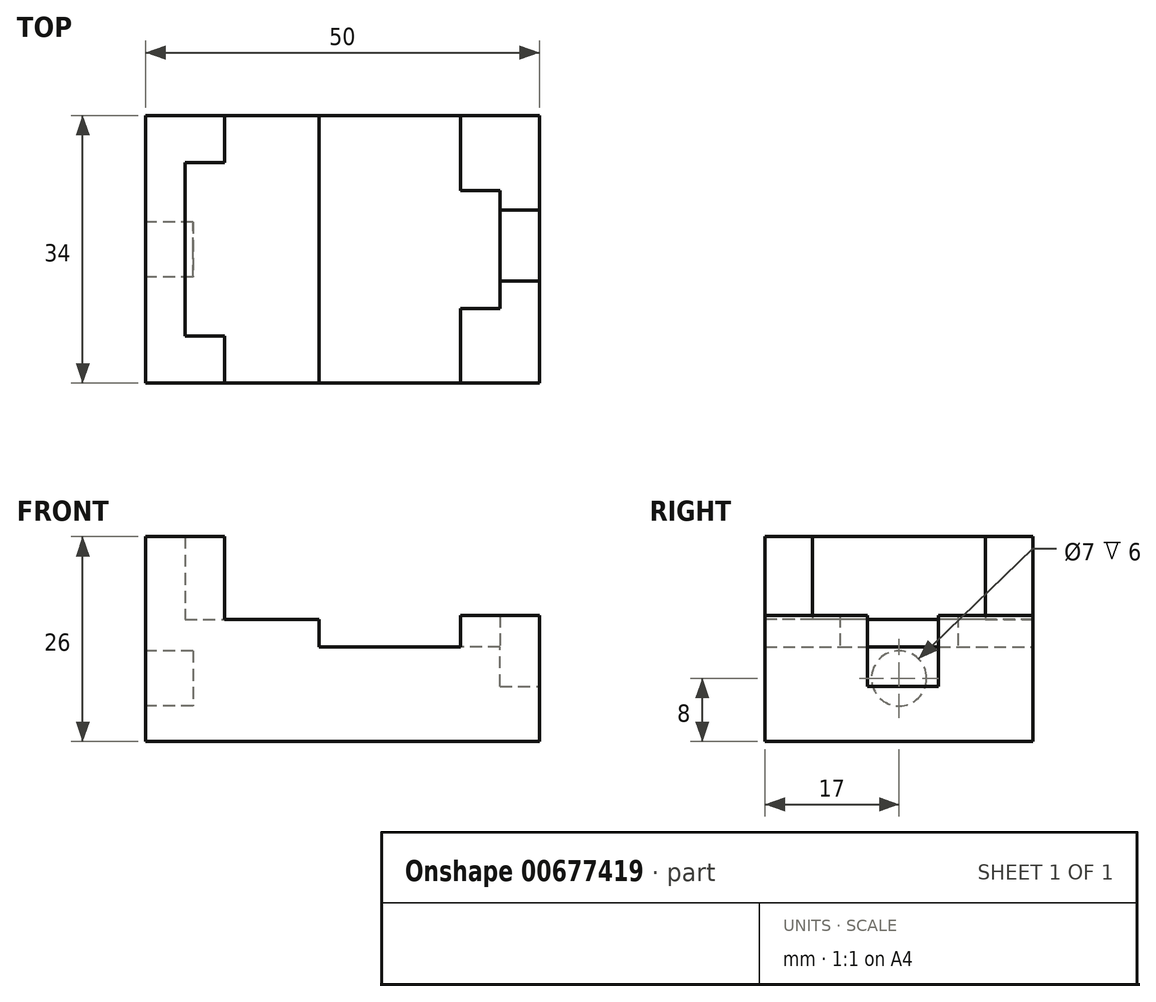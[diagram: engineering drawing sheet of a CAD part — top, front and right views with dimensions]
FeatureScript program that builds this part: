
annotation { "Feature Type Name" : "Feature", "Feature Type Description" : "" }
export const myFeature = defineFeature(function(context is Context, id is Id, definition is map)
    precondition{}
    {
        {
            var Q0;
            Q0=qCreatedBy(makeId("Front.planeOp"),FACE);
            var sketch = newSketch(context, id + "F0", { "sketchPlane" : qUnion([Q0])});
            skLineSegment(sketch, "E0.bottom", {"start": v(-25, 13) * mm, "end": v(0.85, 13) * mm});
            skLineSegment(sketch, "E0.top", {"start": v(-25, -13) * mm, "end": v(25, -13) * mm});
            skLineSegment(sketch, "E0.left", {"start": v(-25, 13) * mm, "end": v(-25, -13) * mm});
            skLineSegment(sketch, "E0.right", {"start": v(25, 3) * mm, "end": v(25, -13) * mm});
            skPoint(sketch, "E0.middle", {"position": v(0, 0) * mm});
            skLineSegment(sketch, "E1.0", {"start": v(0.85, 13) * mm, "end": v(0.85, -1) * mm});
            skLineSegment(sketch, "E2.0", {"start": v(0.85, -1) * mm, "end": v(20, -1) * mm});
            skLineSegment(sketch, "E3.0", {"start": v(20, 3) * mm, "end": v(20, -1) * mm});
            skPoint(sketch, "E4.orphan", {"position": v(25, 13) * mm});
            skLineSegment(sketch, "E5.trimOffspring", {"start": v(20, 3) * mm, "end": v(25, 3) * mm});
            skSolve(sketch);
        }
        {
            var Q0;
            Q0=qSketchRegion(id+"F0",true);
            extrude(context, id + "F1", {"entities" : qUnion([Q0]), "depth" : 34 * mm, "offsetDistance" : 25 * mm});
        }
        {
            var Q0;
            Q0=makeQuery(id+"F1.opExtrude","SWEPT_FACE",FACE,{"disambiguationData":[OSD([sQuery(id+"F0.wireOp",EDGE,"E0.right")])]});
            var sketch = newSketch(context, id + "F2", { "sketchPlane" : qUnion([Q0])});
            skLineSegment(sketch, "E6.bottom", {"start": v(-21, 3) * mm, "end": v(-12, 3) * mm});
            skLineSegment(sketch, "E6.top", {"start": v(-21, -6) * mm, "end": v(-12, -6) * mm});
            skLineSegment(sketch, "E6.left", {"start": v(-21, 3) * mm, "end": v(-21, -6) * mm});
            skLineSegment(sketch, "E7", {"start": v(-12, 3) * mm, "end": v(-12, -6) * mm});
            skSolve(sketch);
        }
        {
            var Q0;
            Q0=qSketchRegion(id+"F2",true);
            var Q1;
            Q1=makeQuery(id+"F1.opExtrude","SWEPT_FACE",FACE,{"disambiguationData":[OSD([sQuery(id+"F0.wireOp",EDGE,"E3.0")])]});
            extrude(context, id + "F3", {"entities" : qUnion([Q0]), "operationType" : NewBodyOperationType.REMOVE, "endBound" : BoundingType.UP_TO_SURFACE, "oppositeDirection" : true, "depth" : 25 * mm, "endBoundEntityFace" : qUnion([Q1]), "offsetDistance" : 25 * mm});
        }
        {
            var Q0;
            Q0=makeQuery(id+"F1.opExtrude","SWEPT_FACE",FACE,{"disambiguationData":[OSD([sQuery(id+"F0.wireOp",EDGE,"E0.left")])]});
            var sketch = newSketch(context, id + "F4", { "sketchPlane" : qUnion([Q0])});
            skCircle(sketch, "E8", {"center": v(17, -5) * mm, "radius": 3.5 * mm});
            skSolve(sketch);
        }
        {
            var Q0;
            Q0=qSketchRegion(id+"F4",true);
            extrude(context, id + "F5", {"entities" : qUnion([Q0]), "operationType" : NewBodyOperationType.REMOVE, "oppositeDirection" : true, "depth" : 6 * mm, "offsetDistance" : 25 * mm});
        }
        {
            var Q0;
            Q0=makeQuery(id+"F3.boolean.opBoolean","MERGE",FACE,{"derivedFrom":[makeQuery(id+"F1.opExtrude","SWEPT_FACE",FACE,{"disambiguationData":[OSD([sQuery(id+"F0.wireOp",EDGE,"E2.0")])]}),makeQuery(id+"F3.opExtrude","SWEPT_FACE",FACE,{"disambiguationData":[OSD([sQuery(id+"F2.wireOp",EDGE,"E6.top")])]})]});
            var sketch = newSketch(context, id + "F6", { "sketchPlane" : qUnion([Q0])});
            skLineSegment(sketch, "E9.bottom", {"start": v(20, -34) * mm, "end": v(15, -34) * mm});
            skLineSegment(sketch, "E9.top", {"start": v(20, -24.5) * mm, "end": v(15, -24.5) * mm});
            skLineSegment(sketch, "E9.left", {"start": v(20, -34) * mm, "end": v(20, -24.5) * mm});
            skLineSegment(sketch, "E9.right", {"start": v(15, -34) * mm, "end": v(15, -24.5) * mm});
            skLineSegment(sketch, "E10.bottom", {"start": v(20, -9.5) * mm, "end": v(15, -9.5) * mm});
            skLineSegment(sketch, "E10.top", {"start": v(20, 0) * mm, "end": v(15, 0) * mm});
            skLineSegment(sketch, "E10.left", {"start": v(20, -9.5) * mm, "end": v(20, 0) * mm});
            skLineSegment(sketch, "E10.right", {"start": v(15, -9.5) * mm, "end": v(15, 0) * mm});
            skSolve(sketch);
        }
        {
            var Q0;
            Q0=qSketchRegion(id+"F6",true);
            var Q1;
            {var subQ0=sQuery(id+"F0.wireOp",EDGE,"E5.trimOffspring");Q1=makeQuery(id+"F3.boolean.opBoolean","SPLIT",FACE,{"disambiguationData":[TD([makeQuery(id+"F3.opExtrude","SWEPT_FACE",FACE,{"disambiguationData":[OSD([sQuery(id+"F2.wireOp",EDGE,"E6.left")])]})])],"derivedFrom":makeQuery(id+"F1.opExtrude","SWEPT_FACE",FACE,{"disambiguationData":[OSD([subQ0])]})});}
            extrude(context, id + "F7", {"entities" : qUnion([Q0]), "operationType" : NewBodyOperationType.ADD, "endBound" : BoundingType.UP_TO_SURFACE, "depth" : 25 * mm, "endBoundEntityFace" : qUnion([Q1]), "offsetDistance" : 25 * mm});
        }
        {
            var Q0;
            Q0=makeQuery(id+"F7.boolean.opBoolean","MERGE",FACE,{"derivedFrom":[makeQuery(id+"F1.opExtrude","CAP_FACE",FACE,{"disambiguationData":[OSD([sQuery(id+"F0.wireOp",EDGE,"E0.bottom"),sQuery(id+"F0.wireOp",EDGE,"E0.top"),sQuery(id+"F0.wireOp",EDGE,"E0.left"),sQuery(id+"F0.wireOp",EDGE,"E0.right"),sQuery(id+"F0.wireOp",EDGE,"E1.0"),sQuery(id+"F0.wireOp",EDGE,"E2.0"),sQuery(id+"F0.wireOp",EDGE,"E3.0"),sQuery(id+"F0.wireOp",EDGE,"E5.trimOffspring")])],"isStart":false}),makeQuery(id+"F7.opExtrude","SWEPT_FACE",FACE,{"disambiguationData":[OSD([sQuery(id+"F6.wireOp",EDGE,"E9.bottom")])]})]});
            var sketch = newSketch(context, id + "F8", { "sketchPlane" : qUnion([Q0])});
            skLineSegment(sketch, "E11.bottom", {"start": v(0.85, 13) * mm, "end": v(-20, 13) * mm});
            skLineSegment(sketch, "E11.top", {"start": v(0.85, -1) * mm, "end": v(-20, -1) * mm});
            skLineSegment(sketch, "E11.left", {"start": v(0.85, 13) * mm, "end": v(0.85, -1) * mm});
            skLineSegment(sketch, "E11.right", {"start": v(-20, 13) * mm, "end": v(-20, -1) * mm});
            skSolve(sketch);
        }
        {
            var Q0;
            Q0 = qSketchRegion(id + "F8", true);
            extrude(context, id + "F9", {"entities" : qUnion([Q0]), "operationType" : NewBodyOperationType.REMOVE, "endBound" : BoundingType.THROUGH_ALL, "oppositeDirection" : true, "depth" : 25 * mm, "offsetDistance" : 25 * mm});
        }
        {
            var Q0;
            Q0=makeQuery(id+"F7.boolean.opBoolean","MERGE",FACE,{"derivedFrom":[makeQuery(id+"F1.opExtrude","CAP_FACE",FACE,{"disambiguationData":[OSD([sQuery(id+"F0.wireOp",EDGE,"E0.bottom"),sQuery(id+"F0.wireOp",EDGE,"E0.top"),sQuery(id+"F0.wireOp",EDGE,"E0.left"),sQuery(id+"F0.wireOp",EDGE,"E0.right"),sQuery(id+"F0.wireOp",EDGE,"E1.0"),sQuery(id+"F0.wireOp",EDGE,"E2.0"),sQuery(id+"F0.wireOp",EDGE,"E3.0"),sQuery(id+"F0.wireOp",EDGE,"E5.trimOffspring")])],"isStart":false}),makeQuery(id+"F7.opExtrude","SWEPT_FACE",FACE,{"disambiguationData":[OSD([sQuery(id+"F6.wireOp",EDGE,"E9.bottom")])]})]});
            var sketch = newSketch(context, id + "F10", { "sketchPlane" : qUnion([Q0])});
            skLineSegment(sketch, "E12.bottom", {"start": v(-20, 13) * mm, "end": v(-15, 13) * mm});
            skLineSegment(sketch, "E12.top", {"start": v(-20, -1) * mm, "end": v(-15, -1) * mm});
            skLineSegment(sketch, "E12.left", {"start": v(-20, 13) * mm, "end": v(-20, -1) * mm});
            skLineSegment(sketch, "E12.right", {"start": v(-15, 13) * mm, "end": v(-15, -1) * mm});
            skSolve(sketch);
        }
        {
            var Q0;
            Q0 = qSketchRegion(id + "F10", true);
            extrude(context, id + "F11", {"entities" : qUnion([Q0]), "operationType" : NewBodyOperationType.ADD, "oppositeDirection" : true, "depth" : 6 * mm, "offsetDistance" : 25 * mm});
        }
        {
            var Q0;
            Q0=makeQuery(id+"F7.boolean.opBoolean","MERGE",FACE,{"derivedFrom":[makeQuery(id+"F1.opExtrude","CAP_FACE",FACE,{"disambiguationData":[OSD([sQuery(id+"F0.wireOp",EDGE,"E0.bottom"),sQuery(id+"F0.wireOp",EDGE,"E0.top"),sQuery(id+"F0.wireOp",EDGE,"E0.left"),sQuery(id+"F0.wireOp",EDGE,"E0.right"),sQuery(id+"F0.wireOp",EDGE,"E1.0"),sQuery(id+"F0.wireOp",EDGE,"E2.0"),sQuery(id+"F0.wireOp",EDGE,"E3.0"),sQuery(id+"F0.wireOp",EDGE,"E5.trimOffspring")])],"isStart":true}),makeQuery(id+"F7.opExtrude","SWEPT_FACE",FACE,{"disambiguationData":[OSD([sQuery(id+"F6.wireOp",EDGE,"E10.top")])]})]});
            var sketch = newSketch(context, id + "F12", { "sketchPlane" : qUnion([Q0])});
            skLineSegment(sketch, "E13.bottom", {"start": v(20, 13) * mm, "end": v(15, 13) * mm});
            skLineSegment(sketch, "E13.top", {"start": v(20, -1) * mm, "end": v(15, -1) * mm});
            skLineSegment(sketch, "E13.left", {"start": v(20, 13) * mm, "end": v(20, -1) * mm});
            skLineSegment(sketch, "E13.right", {"start": v(15, 13) * mm, "end": v(15, -1) * mm});
            skSolve(sketch);
        }
        {
            var Q0;
            Q0 = qSketchRegion(id + "F12", true);
            extrude(context, id + "F13", {"entities" : qUnion([Q0]), "operationType" : NewBodyOperationType.ADD, "oppositeDirection" : true, "depth" : 6 * mm, "offsetDistance" : 25 * mm});
        }
        {
            var Q0;
            Q0=makeQuery(id+"F9.boolean.opBoolean","MERGE",FACE,{"derivedFrom":[makeQuery(id+"F1.opExtrude","SWEPT_FACE",FACE,{"disambiguationData":[OSD([sQuery(id+"F0.wireOp",EDGE,"E2.0")])]}),makeQuery(id+"F9.opExtrude","SWEPT_FACE",FACE,{"disambiguationData":[OSD([sQuery(id+"F8.wireOp",EDGE,"E11.top")])]})]});
            var sketch = newSketch(context, id + "F14", { "sketchPlane" : qUnion([Q0])});
            skLineSegment(sketch, "E14.0.0", {"start": v(-15, 0) * mm, "end": v(-15, -6) * mm});
            skLineSegment(sketch, "E14.0.1", {"start": v(-15, -6) * mm, "end": v(-20, -6) * mm});
            skLineSegment(sketch, "E14.0.2", {"start": v(-20, -6) * mm, "end": v(-20, -28) * mm});
            skLineSegment(sketch, "E14.0.3", {"start": v(-20, -28) * mm, "end": v(-15, -28) * mm});
            skLineSegment(sketch, "E14.0.4", {"start": v(-15, -28) * mm, "end": v(-15, -34) * mm});
            skLineSegment(sketch, "E14.0.5", {"start": v(-15, -34) * mm, "end": v(-3, -34) * mm});
            skLineSegment(sketch, "E14.0.10", {"start": v(20, -12) * mm, "end": v(20, -9.5) * mm});
            skLineSegment(sketch, "E14.0.13", {"start": v(-3, 0) * mm, "end": v(-15, 0) * mm});
            skLineSegment(sketch, "E15", {"start": v(-3, 0) * mm, "end": v(-3, -34) * mm});
            skPoint(sketch, "E14.0.12.end.orphan", {"position": v(15, 0) * mm});
            skPoint(sketch, "E14.0.11.end.orphan", {"position": v(15, -9.5) * mm});
            skPoint(sketch, "E14.0.8.end.orphan", {"position": v(20, -21) * mm});
            skPoint(sketch, "E14.0.7.end.orphan", {"position": v(20, -24.5) * mm});
            skPoint(sketch, "E14.0.6.end.orphan", {"position": v(15, -24.5) * mm});
            skPoint(sketch, "E16.orphan", {"position": v(15, -34) * mm});
            skSolve(sketch);
        }
        {
            var Q0;
            Q0 = qSketchRegion(id + "F14", true);
            extrude(context, id + "F15", {"entities" : qUnion([Q0]), "operationType" : NewBodyOperationType.ADD, "depth" : 3.5 * mm, "offsetDistance" : 25 * mm});
        }
    });
